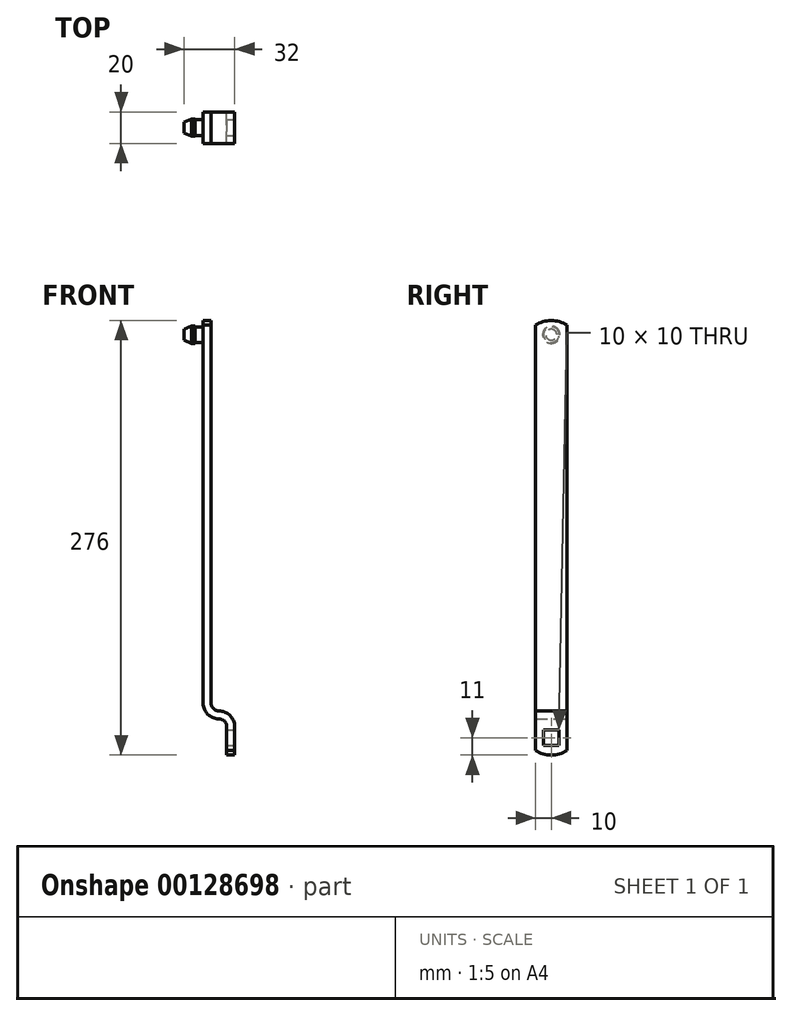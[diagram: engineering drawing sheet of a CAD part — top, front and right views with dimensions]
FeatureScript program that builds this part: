
annotation { "Feature Type Name" : "Feature", "Feature Type Description" : "" }
export const myFeature = defineFeature(function(context is Context, id is Id, definition is map)
    precondition{}
    {
        {
            var Q0;
            Q0=qCreatedBy(makeId("Front.planeOp"),FACE);
            var sketch = newSketch(context, id + "F0", { "sketchPlane" : qUnion([Q0])});
            skLineSegment(sketch, "E0.bottom", {"start": v(2.5, -120) * mm, "end": v(-2.5, -120) * mm});
            skLineSegment(sketch, "E0.top", {"start": v(2.5, 120) * mm, "end": v(-2.5, 120) * mm});
            skLineSegment(sketch, "E0.left", {"start": v(2.5, -120) * mm, "end": v(2.5, 120) * mm});
            skLineSegment(sketch, "E0.right", {"start": v(-2.5, -120) * mm, "end": v(-2.5, 120) * mm});
            skPoint(sketch, "E0.middle", {"position": v(0, 0) * mm});
            skArc(sketch, "E1", {"start": v(2.5, -120) * mm, "mid": v(3.96, -123.54) * mm, "end": v(7.5, -125) * mm});
            skArc(sketch, "E2.0", {"start": v(2.5, -111.34) * mm, "mid": v(-2.16, -122.59) * mm, "end": v(7.5, -130) * mm});
            skLineSegment(sketch, "E3", {"start": v(7.5, -125) * mm, "end": v(7.5, -130) * mm});
            skLineSegment(sketch, "E4", {"start": v(2.5, -120) * mm, "end": v(7.5, -120) * mm, "construction": true});
            skLineSegment(sketch, "E5", {"start": v(7.5, -120) * mm, "end": v(7.5, -125) * mm, "construction": true});
            skArc(sketch, "E6", {"start": v(12.5, -135) * mm, "mid": v(11.04, -131.46) * mm, "end": v(7.5, -130) * mm});
            skArc(sketch, "E7.0", {"start": v(17.5, -135) * mm, "mid": v(11.61, -125.89) * mm, "end": v(0.89, -127.5) * mm});
            skLineSegment(sketch, "E8", {"start": v(12.5, -135) * mm, "end": v(17.5, -135) * mm});
            skLineSegment(sketch, "E9", {"start": v(7.5, -130) * mm, "end": v(7.5, -135) * mm, "construction": true});
            skLineSegment(sketch, "E10.top", {"start": v(12.5, -150) * mm, "end": v(17.5, -150) * mm});
            skLineSegment(sketch, "E10.left", {"start": v(12.5, -135) * mm, "end": v(12.5, -150) * mm});
            skLineSegment(sketch, "E10.right", {"start": v(17.5, -135) * mm, "end": v(17.5, -150) * mm});
            skSolve(sketch);
        }
        {
            var Q0;
            Q0 = qSketchRegion(id + "F0", true);
            extrude(context, id + "F1", {"entities" : qUnion([Q0]), "depth" : 20 * mm});
        }
        {
            var Q0;
            Q0=makeQuery(id+"F1.opExtrude","SWEPT_FACE",FACE,{"disambiguationData":[OSD([sQuery(id+"F0.wireOp",EDGE,"E10.right")])]});
            var sketch = newSketch(context, id + "F2", { "sketchPlane" : qUnion([Q0])});
            skLineSegment(sketch, "E11.bottom", {"start": v(-5, -147) * mm, "end": v(-15, -147) * mm});
            skLineSegment(sketch, "E11.top", {"start": v(-5, -137) * mm, "end": v(-15, -137) * mm});
            skLineSegment(sketch, "E11.left", {"start": v(-5, -147) * mm, "end": v(-5, -137) * mm});
            skLineSegment(sketch, "E11.right", {"start": v(-15, -147) * mm, "end": v(-15, -137) * mm});
            skPoint(sketch, "E11.middle", {"position": v(-10, -142) * mm});
            skPoint(sketch, "E11.middle.positionSnap0", {"position": v(-10, -150) * mm});
            skPoint(sketch, "E11.centerSnap0", {"position": v(-10, -150) * mm});
            skArc(sketch, "E12", {"start": v(-20, -150) * mm, "mid": v(-10, -153) * mm, "end": v(0, -150) * mm});
            skSolve(sketch);
        }
        {
            var Q0;
            Q0=makeQuery(id+"F2.imprint","IMPRINT",FACE,{"disambiguationData":[TD([[makeQuery(id+"F2.imprint","IMPRINT",EDGE,{"derivedFrom":sQuery(id+"F2.wireOp",EDGE,"E12")}),1.0]])]});
            extrude(context, id + "F3", {"entities" : qUnion([Q0]), "operationType" : NewBodyOperationType.ADD, "oppositeDirection" : true, "depth" : 5 * mm});
        }
        {
            var Q0;
            {var subQ0=sQuery(id+"F2.wireOp",EDGE,"E11.top");Q0=makeQuery(id+"F2.imprint","IMPRINT",FACE,{"disambiguationData":[TD([[makeQuery(id+"F2.imprint","IMPRINT",EDGE,{"derivedFrom":subQ0}),1.0]])]});}
            var Q1;
            {var subQ0=sQuery(id+"F2.wireOp",EDGE,"E11.bottom");Q1=makeQuery(id+"F2.imprint","IMPRINT",FACE,{"disambiguationData":[TD([[makeQuery(id+"F2.imprint","IMPRINT",EDGE,{"derivedFrom":subQ0}),-1.0]])]});}
            extrude(context, id + "F4", {"entities" : qUnion([Q0, Q1]), "operationType" : NewBodyOperationType.REMOVE, "endBound" : BoundingType.THROUGH_ALL, "oppositeDirection" : true, "depth" : 25 * mm});
        }
        {
            var Q0;
            Q0=makeQuery(id+"F1.opExtrude","SWEPT_FACE",FACE,{"disambiguationData":[OSD([sQuery(id+"F0.wireOp",EDGE,"E0.right")])]});
            var sketch = newSketch(context, id + "F5", { "sketchPlane" : qUnion([Q0])});
            skArc(sketch, "E13", {"start": v(20, 120) * mm, "mid": v(10, 123) * mm, "end": v(0, 120) * mm});
            skPoint(sketch, "E14", {"position": v(10, 120) * mm});
            skCircle(sketch, "E15", {"center": v(10, 114) * mm, "radius": 5 * mm});
            skSolve(sketch);
        }
        {
            var Q0;
            Q0=makeQuery(id+"F5.imprint","IMPRINT",FACE,{"disambiguationData":[TD([[makeQuery(id+"F5.imprint","IMPRINT",EDGE,{"derivedFrom":sQuery(id+"F5.wireOp",EDGE,"E13")}),1.0]])]});
            extrude(context, id + "F6", {"entities" : qUnion([Q0]), "operationType" : NewBodyOperationType.ADD, "oppositeDirection" : true, "depth" : 5 * mm});
        }
        {
            var Q0;
            Q0=makeQuery(id+"F5.imprint","IMPRINT",FACE,{"disambiguationData":[TD([[makeQuery(id+"F5.imprint","IMPRINT",EDGE,{"derivedFrom":sQuery(id+"F5.wireOp",EDGE,"E15")}),1.0]])]});
            extrude(context, id + "F7", {"entities" : qUnion([Q0]), "operationType" : NewBodyOperationType.ADD, "depth" : 5 * mm});
        }
        {
            var Q0;
            Q0=makeQuery(id+"F7.opExtrude","CAP_FACE",FACE,{"disambiguationData":[OSD([sQuery(id+"F5.wireOp",EDGE,"E15")])],"isStart":false});
            var sketch = newSketch(context, id + "F8", { "sketchPlane" : qUnion([Q0])});
            skCircle(sketch, "E16", {"center": v(10, 114) * mm, "radius": 5.5 * mm});
            skSolve(sketch);
        }
        {
            var Q0;
            Q0=makeQuery(id+"F8.imprint","IMPRINT",FACE,{"disambiguationData":[TD([[makeQuery(id+"F8.imprint","IMPRINT",EDGE,{"derivedFrom":sQuery(id+"F8.wireOp",EDGE,"E16")}),1.0]])]});
            var Q1;
            Q1=makeQuery(id+"F8.imprint","IMPRINT",FACE,{"disambiguationData":[TD([[makeQuery(id+"F8.imprint","IMPRINT",EDGE,{"derivedFrom":makeQuery(id+"F7.opExtrude","CAP_EDGE",EDGE,{"disambiguationData":[OSD([sQuery(id+"F5.wireOp",EDGE,"E15")])],"isStart":false})}),1.0]])]});
            extrude(context, id + "F9", {"entities" : qUnion([Q0, Q1]), "operationType" : NewBodyOperationType.ADD, "depth" : 2.5 * mm});
        }
        {
            var Q0;
            Q0=makeQuery(id+"F9.opExtrude","CAP_FACE",FACE,{"disambiguationData":[OSD([sQuery(id+"F8.wireOp",EDGE,"E16")])],"isStart":false});
            cPlane(context, id + "F10", {"entities" : qUnion([Q0]), "cplaneType" : CPlaneType.OFFSET, "offset" : 4.5 * mm, "width" : 150 * mm, "height" : 150 * mm});
        }
        {
            var Q0;
            Q0=qCreatedBy(id+"F10.planeOp",FACE);
            var sketch = newSketch(context, id + "F11", { "sketchPlane" : qUnion([Q0])});
            skCircle(sketch, "E17.0", {"center": v(10, 114) * mm, "radius": 5.5 * mm});
            skCircle(sketch, "E18", {"center": v(10, 114) * mm, "radius": 3.5 * mm});
            skSolve(sketch);
        }
        {
            var Q1;
            Q1=makeQuery(id+"F11.imprint","IMPRINT",FACE,{"disambiguationData":[TD([[makeQuery(id+"F11.imprint","IMPRINT",EDGE,{"derivedFrom":sQuery(id+"F11.wireOp",EDGE,"E18")}),1.0]])]});
            var Q2;
            Q2=makeQuery(id+"F9.opExtrude","CAP_FACE",FACE,{"disambiguationData":[OSD([sQuery(id+"F8.wireOp",EDGE,"E16")])],"isStart":false});
            loft(context, id + "F12", {"operationType" : NewBodyOperationType.ADD, "sheetProfilesArray" : [{ "sheetProfileEntities" : qUnion([Q1]) }, { "sheetProfileEntities" : qUnion([Q2]) }]});
        }
    });
